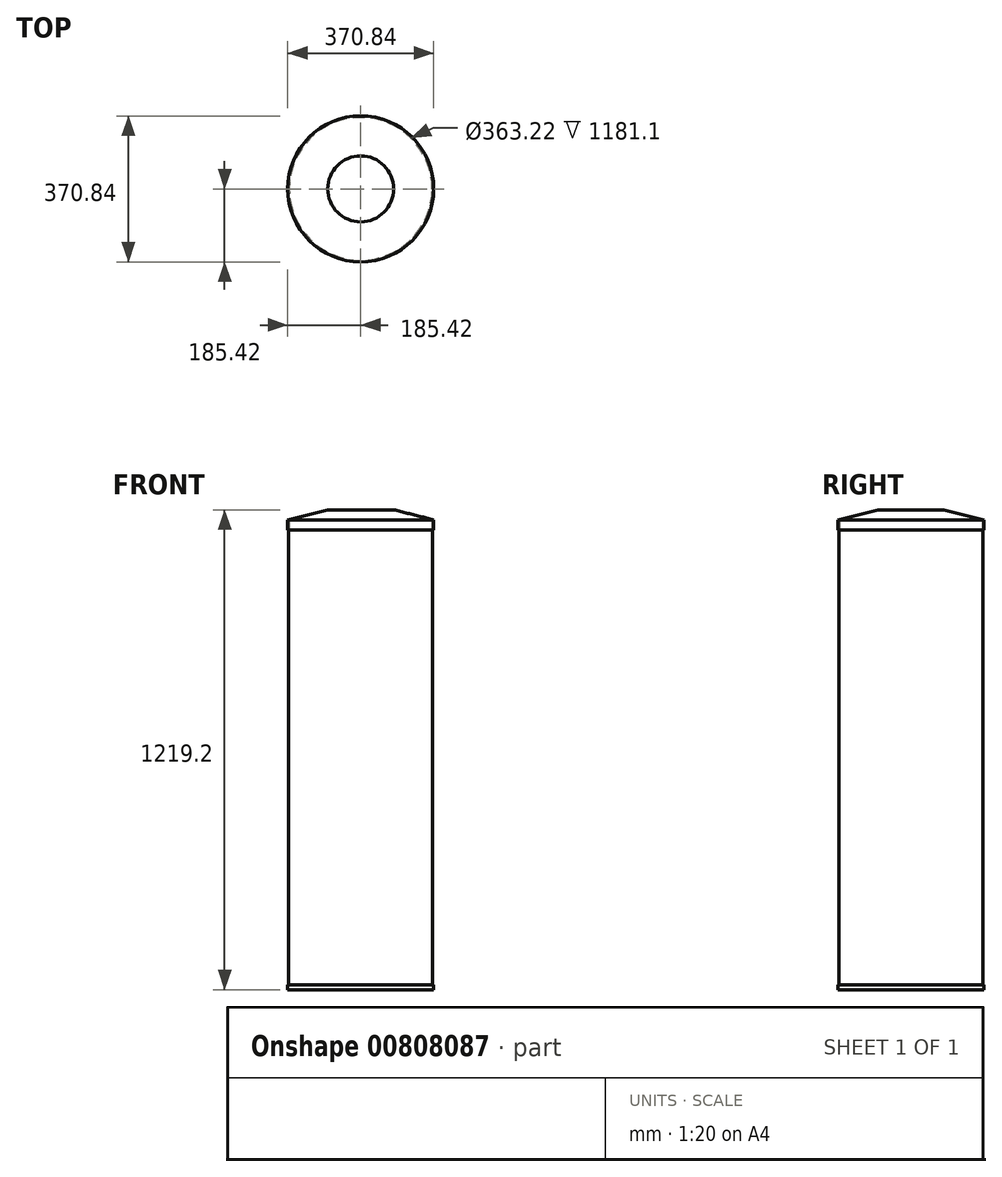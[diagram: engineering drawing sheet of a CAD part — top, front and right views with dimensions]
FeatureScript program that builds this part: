
annotation { "Feature Type Name" : "Feature", "Feature Type Description" : "" }
export const myFeature = defineFeature(function(context is Context, id is Id, definition is map)
    precondition{}
    {
        {
            var Q0;
            Q0=qCreatedBy(makeId("Top.planeOp"),FACE);
            var sketch = newSketch(context, id + "F0", { "sketchPlane" : qUnion([Q0])});
            skCircle(sketch, "E0", {"center": v(0, 0) * mm, "radius": 185.42 * mm});
            skSolve(sketch);
        }
        {
            var Q0;
            Q0=makeQuery(id+"F0.imprint","IMPRINT",FACE,{"disambiguationData":[TD([[makeQuery(id+"F0.imprint","IMPRINT",EDGE,{"derivedFrom":sQuery(id+"F0.wireOp",EDGE,"E0")}),1.0]])]});
            extrude(context, id + "F1", {"entities" : qUnion([Q0]), "depth" : 12.7 * mm, "offsetDistance" : 25.4 * mm});
        }
        {
            var Q0;
            Q0=makeQuery(id+"F1.opExtrude","CAP_FACE",FACE,{"disambiguationData":[OSD([sQuery(id+"F0.wireOp",EDGE,"E0")])],"isStart":false});
            var sketch = newSketch(context, id + "F2", { "sketchPlane" : qUnion([Q0])});
            skCircle(sketch, "E1", {"center": v(0, 0) * mm, "radius": 182.88 * mm});
            skCircle(sketch, "E2", {"center": v(0, 0) * mm, "radius": 181.61 * mm});
            skSolve(sketch);
        }
        {
            var Q0;
            Q0 = qSketchRegion(id + "F2", true);
            extrude(context, id + "F3", {"entities" : qUnion([Q0]), "operationType" : NewBodyOperationType.ADD, "depth" : 1181.1 * mm, "offsetDistance" : 25.4 * mm});
        }
        {
            var Q0;
            Q0=makeQuery(id+"F3.opExtrude","CAP_FACE",FACE,{"disambiguationData":[OSD([sQuery(id+"F2.wireOp",EDGE,"E1"),sQuery(id+"F2.wireOp",EDGE,"E2")])],"isStart":false});
            var sketch = newSketch(context, id + "F4", { "sketchPlane" : qUnion([Q0])});
            skCircle(sketch, "E3", {"center": v(0, 0) * mm, "radius": 185.42 * mm});
            skSolve(sketch);
        }
        {
            var Q0;
            Q0 = qSketchRegion(id + "F4", true);
            extrude(context, id + "F5", {"entities" : qUnion([Q0]), "operationType" : NewBodyOperationType.ADD, "depth" : 25.4 * mm, "offsetDistance" : 25.4 * mm});
        }
        {
            var Q0;
            Q0=makeQuery(id+"F5.opExtrude","CAP_EDGE",EDGE,{"disambiguationData":[OSD([sQuery(id+"F4.wireOp",EDGE,"E3")])],"isStart":false});
            chamfer(context, id + "F6", {"entities" : qUnion([Q0]), "chamferType" : ChamferType.TWO_OFFSETS, "width1" : 101.6 * mm, "oppositeDirection" : false, "width2" : 25.4 * mm});
        }
        {
            var Q0;
            {var subQ0=sQuery(id+"F4.wireOp",EDGE,"E3");Q0=makeQuery(id+"F5.boolean.opBoolean","SPLIT",FACE,{"disambiguationData":[TD([makeQuery(id+"F3.opExtrude","SWEPT_FACE",FACE,{"disambiguationData":[OSD([sQuery(id+"F2.wireOp",EDGE,"E1")])]})])],"derivedFrom":makeQuery(id+"F5.opExtrude","CAP_FACE",FACE,{"disambiguationData":[OSD([subQ0])],"isStart":true})});}
            var sketch = newSketch(context, id + "F7", { "sketchPlane" : qUnion([Q0])});
            skCircle(sketch, "E4.0", {"center": v(0, 0) * mm, "radius": 182.88 * mm});
            skCircle(sketch, "E5.0.0", {"center": v(0, 0) * mm, "radius": 185.42 * mm});
            skSolve(sketch);
        }
        {
            var Q0;
            Q0 = qSketchRegion(id + "F7", true);
            extrude(context, id + "F8", {"entities" : qUnion([Q0]), "operationType" : NewBodyOperationType.ADD, "depth" : 25.4 * mm, "offsetDistance" : 25.4 * mm});
        }
    });
